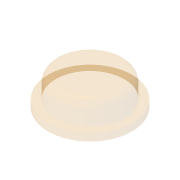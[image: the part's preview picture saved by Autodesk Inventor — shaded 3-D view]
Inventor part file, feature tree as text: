
AUTODESK INVENTOR PART (.ipt)
format: ipt  version: 2016 SP1 (Build 200210100, 210)  size: 100,352 bytes
history: native  units: mm
features: extrude x2, sketch x2, fillet x1
ambient origin geometry x8: Origin, YZ Plane, XZ Plane, XY Plane, X Axis, Y Axis, Z Axis, Center Point
bodies: Volumenkörper1 (feature_tree)
feature tree (5):
  extrude  "Extrusion1"  Depth=0.85mm TaperAngle=0.0deg
  extrude  "Extrusion2"  Depth=2.65mm TaperAngle=0.0deg
  fillet  "Rundung1"  Radius=1.0mm
  sketch  "Skizze1"  dims[d0=9.8mm d1=0.85mm d2=0.0mm]
  sketch  "Skizze2"  dims[d3=8.0mm d4=2.65mm d5=0.0mm d6=1.0mm]
